# Revit family: Shaving_Mirror-Grohe-40808000
name_source: partatom
category: Specialty Equipment
revit_build: Autodesk Revit 2018 (Build: 20170223_1515(x64)
units: mm (PartAtom-declared; Revit-internal decimal feet)

## family parameters
Cut with Voids When Loaded = No
Host = Face
OmniClass Number = 23.40.95.17.17
OmniClass Title = Mirrors
Part Type = Normal
Room Calculation Point = No
Round Connector Dimension = Use Diameter
Shared = Yes

## types (1)
- 40808000
    Assembly Code = E1090900
    Body Material = Metal-Grohe-000-Starlight Chrome
    Default Elevation = 0 cm
    Description = SELECTION CUBE Shaving Glass
    Height = 18 cm
    Installation Type = Wall Mounted
    Length = 22 cm
    Manufacturer = Grohe
    Material = Metal-Grohe-000-Starlight Chrome
    Model = 40808000
    Price = Prices may vary. Please consult Manufacturer Representative for most up-to-date price list.
    Product Documentation Link = https://americanstandard.box.com
    Product Page URL = https://www.grohe.us
    Region = North America
    URL = https://www.grohe.us
    Warranty Information = Lifetime Limited Warranty
    Width = 19 cm

## geometry (parser evidence)
native form markers: Sweep x3
no freeform markers — native parametric forms only
